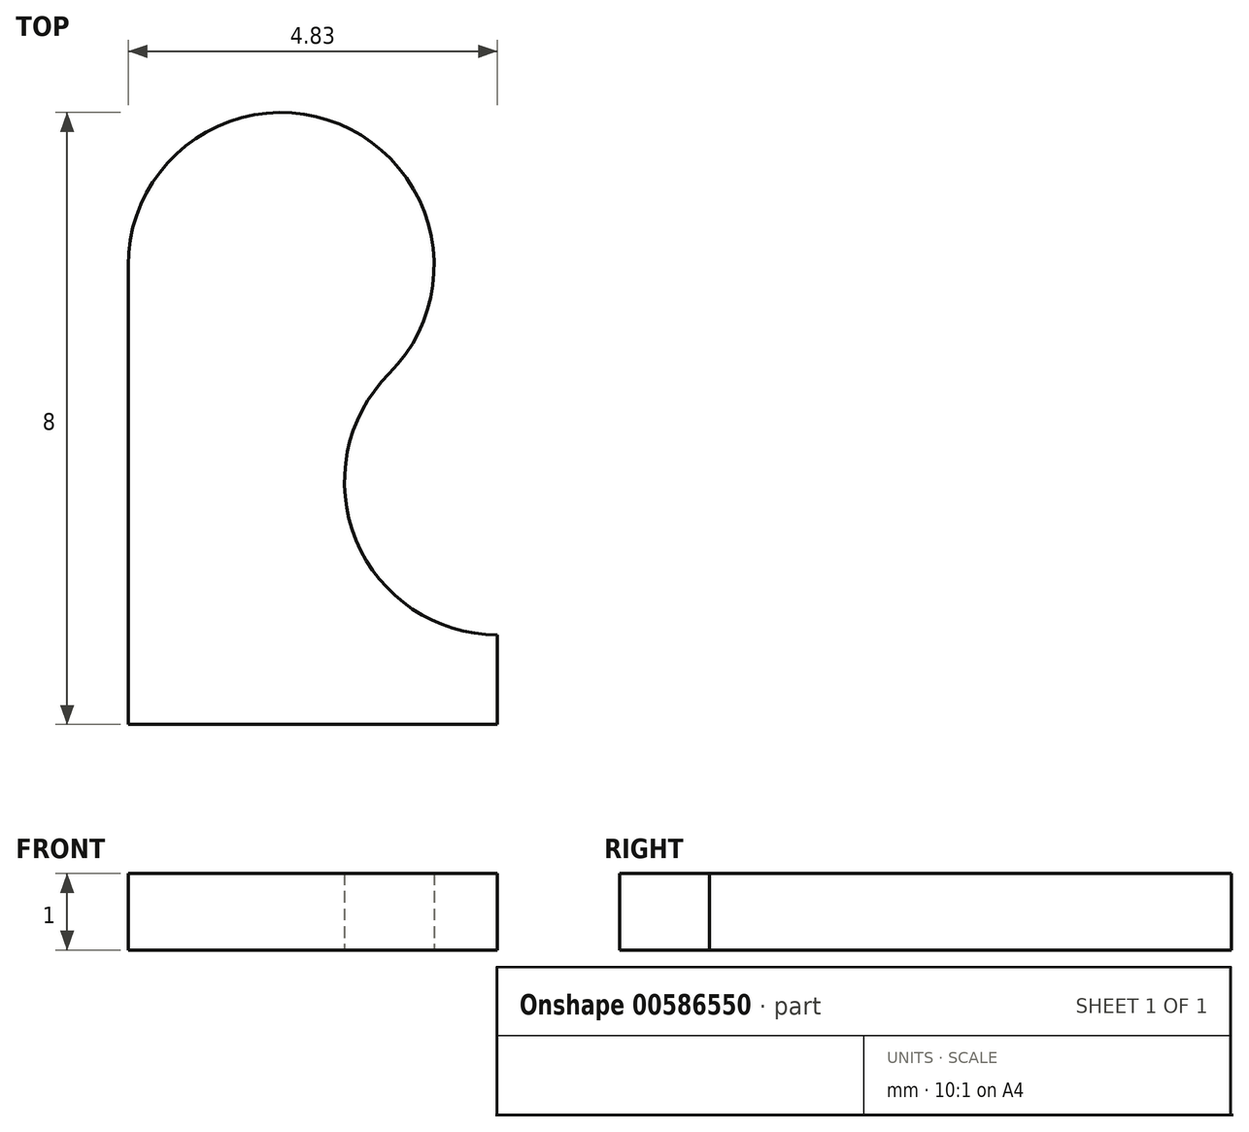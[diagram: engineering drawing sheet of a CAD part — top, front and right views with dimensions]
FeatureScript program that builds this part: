
annotation { "Feature Type Name" : "Feature", "Feature Type Description" : "" }
export const myFeature = defineFeature(function(context is Context, id is Id, definition is map)
    precondition{}
    {
        {
            var Q0;
            Q0=qCreatedBy(makeId("Top.planeOp"),FACE);
            var sketch = newSketch(context, id + "F0", { "sketchPlane" : qUnion([Q0])});
            skLineSegment(sketch, "E0", {"start": v(0, 0) * mm, "end": v(0, 6) * mm});
            skArc(sketch, "E1", {"start": v(0, 6) * mm, "mid": v(2.77, 7.85) * mm, "end": v(3.41, 4.59) * mm});
            skArc(sketch, "E2", {"start": v(3.41, 4.59) * mm, "mid": v(2.98, 2.4) * mm, "end": v(4.83, 1.17) * mm});
            skLineSegment(sketch, "E3", {"start": v(2, 6) * mm, "end": v(4.83, 3.17) * mm, "construction": true});
            skLineSegment(sketch, "E4", {"start": v(4.83, 0) * mm, "end": v(4.83, 3.17) * mm, "construction": true});
            skLineSegment(sketch, "E5", {"start": v(0, 0) * mm, "end": v(4.83, 0) * mm});
            skLineSegment(sketch, "E6", {"start": v(4.83, 1.17) * mm, "end": v(4.83, 0) * mm});
            skLineSegment(sketch, "E7", {"start": v(0, 6) * mm, "end": v(2, 6) * mm, "construction": true});
            skLineSegment(sketch, "E8", {"start": v(2, 6) * mm, "end": v(2, 4) * mm, "construction": true});
            skLineSegment(sketch, "E9", {"start": v(2, 4) * mm, "end": v(2, 2) * mm, "construction": true});
            skLineSegment(sketch, "E10", {"start": v(2, 0) * mm, "end": v(2, 2) * mm, "construction": true});
            skSolve(sketch);
        }
        {
            var Q0;
            Q0=qSketchRegion(id+"F0",true);
            extrude(context, id + "F1", {"entities" : qUnion([Q0]), "depth" : 1 * mm, "offsetDistance" : 25 * mm});
        }
    });
